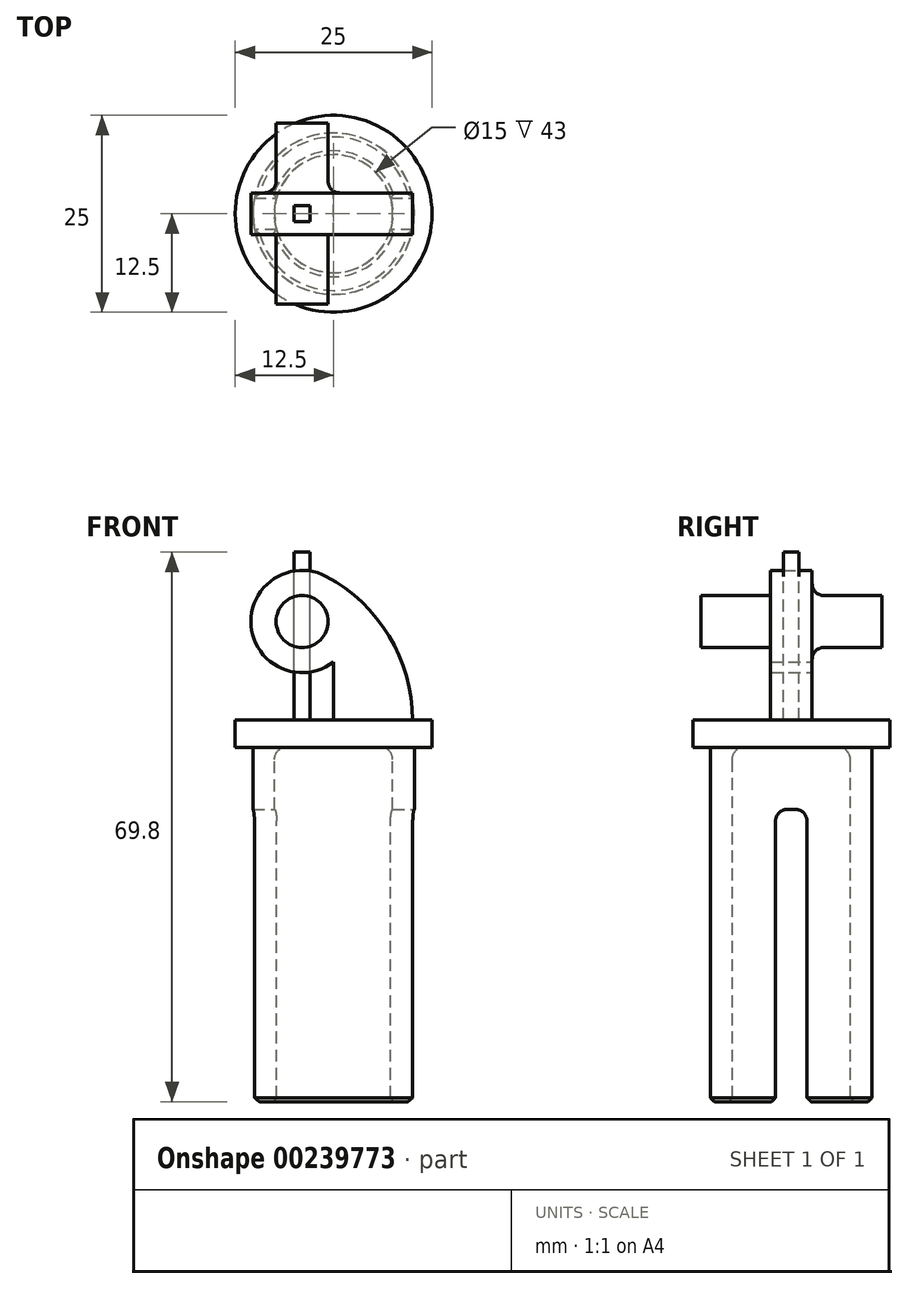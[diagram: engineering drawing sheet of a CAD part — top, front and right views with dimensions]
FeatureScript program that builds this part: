
annotation { "Feature Type Name" : "Feature", "Feature Type Description" : "" }
export const myFeature = defineFeature(function(context is Context, id is Id, definition is map)
    precondition{}
    {
        {
            var Q0;
            Q0=qCreatedBy(makeId("Front.planeOp"),FACE);
            var sketch = newSketch(context, id + "F0", { "sketchPlane" : qUnion([Q0])});
            skCircle(sketch, "E0", {"center": v(-4, 12.5) * mm, "radius": 3.3 * mm});
            skCircle(sketch, "E1", {"center": v(-4, 12.5) * mm, "radius": 6.5 * mm});
            skLineSegment(sketch, "E2.bottom", {"start": v(-4, 12.5) * mm, "end": v(0, 12.5) * mm});
            skLineSegment(sketch, "E2.top", {"start": v(-4, 0) * mm, "end": v(0, 0) * mm});
            skLineSegment(sketch, "E2.left", {"start": v(-4, 12.5) * mm, "end": v(-4, 0) * mm});
            skLineSegment(sketch, "E2.right", {"start": v(0, 12.5) * mm, "end": v(0, 0) * mm});
            skLineSegment(sketch, "E3.bottom", {"start": v(-4, 0) * mm, "end": v(10, 0) * mm});
            skLineSegment(sketch, "E3.top", {"start": v(-4, 19) * mm, "end": v(10, 19) * mm});
            skLineSegment(sketch, "E3.left", {"start": v(-4, 0) * mm, "end": v(-4, 19) * mm});
            skLineSegment(sketch, "E3.right", {"start": v(10, 0) * mm, "end": v(10, 19) * mm});
            skCircle(sketch, "E4", {"center": v(-10.67, 0) * mm, "radius": 20.67 * mm});
            skLineSegment(sketch, "E5", {"start": v(0, -28.46) * mm, "end": v(0, 52.46) * mm, "construction": true});
            skLineSegment(sketch, "E6", {"start": v(-4, 12.5) * mm, "end": v(0, 12.5) * mm, "construction": true});
            skLineSegment(sketch, "E7", {"start": v(-54.91, 0) * mm, "end": v(33.58, 0) * mm, "construction": true});
            skSolve(sketch);
        }
        {
            var Q0;
            {var subQ3=sQuery(id+"F0.wireOp",EDGE,"E4");var subQ6=sQuery(id+"F0.wireOp",EDGE,"E1");var subQ9=makeQuery(id+"F0.imprint","INTERSECT",VERTEX,{"derivedFrom":[subQ6,subQ3]});Q0=makeQuery(id+"F0.imprint","IMPRINT",FACE,{"disambiguationData":[TD([[makeQuery(id+"F0.imprint","IMPRINT",EDGE,{"disambiguationData":[TD([[subQ9,1.0]])],"derivedFrom":subQ6}),-1.0]])]});}
            var Q1;
            {var subQ3=sQuery(id+"F0.wireOp",EDGE,"E0");var subQ8=sQuery(id+"F0.wireOp",EDGE,"E3.left");var subQ10=makeQuery(id+"F0.imprint","INTERSECT",VERTEX,{"disambiguationData":[OD(0.0)],"derivedFrom":[subQ3,subQ8]});Q1=makeQuery(id+"F0.imprint","IMPRINT",FACE,{"disambiguationData":[TD([[makeQuery(id+"F0.imprint","IMPRINT",EDGE,{"disambiguationData":[TD([[subQ10,1.0]])],"derivedFrom":subQ3}),-1.0]])]});}
            var Q2;
            {var subQ1=sQuery(id+"F0.wireOp",EDGE,"E2.bottom");var subQ5=sQuery(id+"F0.wireOp",EDGE,"E0");var subQ6=makeQuery(id+"F0.imprint","INTERSECT",VERTEX,{"derivedFrom":[subQ5,subQ1]});Q2=makeQuery(id+"F0.imprint","IMPRINT",FACE,{"disambiguationData":[TD([[makeQuery(id+"F0.imprint","IMPRINT",EDGE,{"disambiguationData":[TD([[subQ6,1.0]])],"derivedFrom":subQ5}),-1.0]])]});}
            var Q3;
            {var subQ0=sQuery(id+"F0.wireOp",EDGE,"E3.left");var subQ1=sQuery(id+"F0.wireOp",EDGE,"E0");var subQ2=makeQuery(id+"F0.imprint","INTERSECT",VERTEX,{"disambiguationData":[OD(0.0)],"derivedFrom":[subQ1,subQ0]});Q3=makeQuery(id+"F0.imprint","IMPRINT",FACE,{"disambiguationData":[TD([[makeQuery(id+"F0.imprint","IMPRINT",EDGE,{"disambiguationData":[TD([[subQ2,-1.0]])],"derivedFrom":subQ1}),-1.0]])]});}
            extrude(context, id + "F1", {"entities" : qUnion([Q0, Q1, Q2, Q3]), "endBound" : BoundingType.SYMMETRIC, "depth" : 5.3 * mm});
        }
        {
            var Q0;
            {var subQ0=sQuery(id+"F0.wireOp",EDGE,"E2.bottom");var subQ1=sQuery(id+"F0.wireOp",EDGE,"E0");var subQ2=makeQuery(id+"F0.imprint","INTERSECT",VERTEX,{"derivedFrom":[subQ1,subQ0]});Q0=makeQuery(id+"F0.imprint","IMPRINT",FACE,{"disambiguationData":[TD([[makeQuery(id+"F0.imprint","IMPRINT",EDGE,{"disambiguationData":[TD([[subQ2,1.0]])],"derivedFrom":subQ1}),1.0]])]});}
            var Q1;
            {var subQ0=sQuery(id+"F0.wireOp",EDGE,"E3.left");var subQ1=sQuery(id+"F0.wireOp",EDGE,"E0");var subQ2=makeQuery(id+"F0.imprint","INTERSECT",VERTEX,{"disambiguationData":[OD(0.0)],"derivedFrom":[subQ1,subQ0]});Q1=makeQuery(id+"F0.imprint","IMPRINT",FACE,{"disambiguationData":[TD([[makeQuery(id+"F0.imprint","IMPRINT",EDGE,{"disambiguationData":[TD([[subQ2,1.0]])],"derivedFrom":subQ1}),1.0]])]});}
            var Q2;
            {var subQ0=sQuery(id+"F0.wireOp",EDGE,"E3.left");var subQ1=sQuery(id+"F0.wireOp",EDGE,"E0");var subQ2=makeQuery(id+"F0.imprint","INTERSECT",VERTEX,{"disambiguationData":[OD(0.0)],"derivedFrom":[subQ1,subQ0]});Q2=makeQuery(id+"F0.imprint","IMPRINT",FACE,{"disambiguationData":[TD([[makeQuery(id+"F0.imprint","IMPRINT",EDGE,{"disambiguationData":[TD([[subQ2,-1.0]])],"derivedFrom":subQ1}),1.0]])]});}
            extrude(context, id + "F2", {"entities" : qUnion([Q0, Q1, Q2]), "operationType" : NewBodyOperationType.ADD, "endBound" : BoundingType.SYMMETRIC, "depth" : 23 * mm});
        }
        {
            var Q0;
            Q0=qCreatedBy(makeId("Top.planeOp"),FACE);
            var sketch = newSketch(context, id + "F3", { "sketchPlane" : qUnion([Q0])});
            skCircle(sketch, "E8", {"center": v(0, 0) * mm, "radius": 12.5 * mm});
            skSolve(sketch);
        }
        {
            var Q0;
            Q0=makeQuery(id+"F3.imprint","IMPRINT",FACE,{"disambiguationData":[TD([[makeQuery(id+"F3.imprint","IMPRINT",EDGE,{"derivedFrom":sQuery(id+"F3.wireOp",EDGE,"E8")}),1.0]])]});
            extrude(context, id + "F4", {"entities" : qUnion([Q0]), "operationType" : NewBodyOperationType.ADD, "oppositeDirection" : true, "depth" : 3.5 * mm});
        }
        {
            var Q0;
            Q0=makeQuery(id+"F4.opExtrude","CAP_FACE",FACE,{"disambiguationData":[OSD([sQuery(id+"F3.wireOp",EDGE,"E8")])],"isStart":false});
            var sketch = newSketch(context, id + "F5", { "sketchPlane" : qUnion([Q0])});
            skCircle(sketch, "E9", {"center": v(0, 0) * mm, "radius": 10.25 * mm});
            skCircle(sketch, "E10", {"center": v(0, 0) * mm, "radius": 7.5 * mm});
            skSolve(sketch);
        }
        {
            var Q0;
            Q0=makeQuery(id+"F5.imprint","IMPRINT",FACE,{"disambiguationData":[TD([[makeQuery(id+"F5.imprint","IMPRINT",EDGE,{"derivedFrom":sQuery(id+"F5.wireOp",EDGE,"E9")}),1.0]])]});
            extrude(context, id + "F6", {"entities" : qUnion([Q0]), "operationType" : NewBodyOperationType.ADD, "depth" : 45 * mm, "offsetDistance" : 25 * mm});
        }
        {
            var Q0;
            Q0=qCreatedBy(makeId("Front.planeOp"),FACE);
            var sketch = newSketch(context, id + "F7", { "sketchPlane" : qUnion([Q0])});
            skLineSegment(sketch, "E11.bottom", {"start": v(-22.97, -55.7) * mm, "end": v(29.36, -55.7) * mm});
            skLineSegment(sketch, "E11.top", {"start": v(-22.97, -11.36) * mm, "end": v(29.36, -11.36) * mm});
            skLineSegment(sketch, "E11.left", {"start": v(-22.97, -55.7) * mm, "end": v(-22.97, -11.36) * mm});
            skLineSegment(sketch, "E11.right", {"start": v(29.36, -55.7) * mm, "end": v(29.36, -11.36) * mm});
            skSolve(sketch);
        }
        {
            var Q0;
            Q0=makeQuery(id+"F7.imprint","IMPRINT",FACE,{"disambiguationData":[TD([[makeQuery(id+"F7.imprint","IMPRINT",EDGE,{"derivedFrom":sQuery(id+"F7.wireOp",EDGE,"E11.bottom")}),1.0]])]});
            extrude(context, id + "F8", {"entities" : qUnion([Q0]), "operationType" : NewBodyOperationType.REMOVE, "endBound" : BoundingType.SYMMETRIC, "depth" : 4 * mm, "offsetDistance" : 25 * mm});
        }
        {
            var Q0;
            Q0=makeQuery(id+"F1.opExtrude","CAP_EDGE",EDGE,{"disambiguationData":[OSD([sQuery(id+"F0.wireOp",EDGE,"E3.bottom")])],"isStart":false});
            var Q1;
            Q1=makeQuery(id+"F1.opExtrude","CAP_EDGE",EDGE,{"disambiguationData":[OSD([sQuery(id+"F0.wireOp",EDGE,"E0")])],"isStart":false});
            var Q2;
            Q2=makeQuery(id+"F1.opExtrude","CAP_EDGE",EDGE,{"disambiguationData":[OSD([sQuery(id+"F0.wireOp",EDGE,"E0")])],"isStart":true});
            var Q3;
            Q3=makeQuery(id+"F1.opExtrude","SWEPT_EDGE",EDGE,{"disambiguationData":[OSD([sQuery(id+"F0.wireOp",EDGE,"E2.right"),sQuery(id+"F0.wireOp",EDGE,"E3.bottom")])]});
            var Q4;
            Q4=makeQuery(id+"F6.opExtrude","CAP_EDGE",EDGE,{"disambiguationData":[OSD([sQuery(id+"F5.wireOp",EDGE,"E9")])],"isStart":true});
            var Q5;
            Q5=makeQuery(id+"F1.opExtrude","CAP_EDGE",EDGE,{"disambiguationData":[OSD([sQuery(id+"F0.wireOp",EDGE,"E3.bottom")])],"isStart":true});
            var Q6;
            Q6=makeQuery(id+"F1.opExtrude","SWEPT_EDGE",EDGE,{"disambiguationData":[OSD([sQuery(id+"F0.wireOp",EDGE,"E3.bottom"),sQuery(id+"F0.wireOp",EDGE,"E3.right"),sQuery(id+"F0.wireOp",EDGE,"E4")])]});
            var Q7;
            Q7=makeQuery(id+"F6.boolean.opBoolean","SPLIT",FACE,{"disambiguationData":[TD([makeQuery(id+"F6.opExtrude","SWEPT_FACE",FACE,{"disambiguationData":[OSD([sQuery(id+"F5.wireOp",EDGE,"E10")])]})])],"derivedFrom":makeQuery(id+"F4.opExtrude","CAP_FACE",FACE,{"disambiguationData":[OSD([sQuery(id+"F3.wireOp",EDGE,"E8")])],"isStart":false})});
            var Q8;
            Q8=makeQuery(id+"F8.boolean.opBoolean","COPY",EDGE,{"disambiguationData":[OD(0.0)],"derivedFrom":makeQuery(id+"F8.opExtrude","CAP_EDGE",EDGE,{"disambiguationData":[OSD([sQuery(id+"F7.wireOp",EDGE,"E11.top")])],"isStart":true})});
            var Q9;
            Q9=makeQuery(id+"F8.boolean.opBoolean","COPY",EDGE,{"disambiguationData":[OD(0.0)],"derivedFrom":makeQuery(id+"F8.opExtrude","CAP_EDGE",EDGE,{"disambiguationData":[OSD([sQuery(id+"F7.wireOp",EDGE,"E11.top")])],"isStart":false})});
            var Q10;
            Q10=makeQuery(id+"F8.boolean.opBoolean","COPY",EDGE,{"disambiguationData":[OD(1.0)],"derivedFrom":makeQuery(id+"F8.opExtrude","CAP_EDGE",EDGE,{"disambiguationData":[OSD([sQuery(id+"F7.wireOp",EDGE,"E11.top")])],"isStart":false})});
            var Q11;
            Q11=makeQuery(id+"F8.boolean.opBoolean","COPY",EDGE,{"disambiguationData":[OD(1.0)],"derivedFrom":makeQuery(id+"F8.opExtrude","CAP_EDGE",EDGE,{"disambiguationData":[OSD([sQuery(id+"F7.wireOp",EDGE,"E11.top")])],"isStart":true})});
            fillet(context, id + "F9", {"entities" : qUnion([Q0, Q1, Q2, Q3, Q4, Q5, Q6, Q7, Q8, Q9, Q10, Q11]), "radius" : 1.5 * mm, "tangentPropagation" : true, "allowEdgeOverflow" : false});
        }
        {
            var Q0;
            {var subQ0=sQuery(id+"F5.wireOp",EDGE,"E9");var subQ1=sQuery(id+"F5.wireOp",EDGE,"E10");Q0=makeQuery(id+"F8.boolean.opBoolean","SPLIT",FACE,{"disambiguationData":[TD([makeQuery(id+"F8.opExtrude","CAP_FACE",FACE,{"disambiguationData":[OSD([sQuery(id+"F7.wireOp",EDGE,"E11.bottom"),sQuery(id+"F7.wireOp",EDGE,"E11.top"),sQuery(id+"F7.wireOp",EDGE,"E11.left"),sQuery(id+"F7.wireOp",EDGE,"E11.right")])],"isStart":true})])],"derivedFrom":makeQuery(id+"F6.opExtrude","CAP_FACE",FACE,{"disambiguationData":[OSD([subQ0,subQ1])],"isStart":false})});}
            var Q1;
            {var subQ0=sQuery(id+"F5.wireOp",EDGE,"E9");var subQ1=sQuery(id+"F5.wireOp",EDGE,"E10");Q1=makeQuery(id+"F8.boolean.opBoolean","SPLIT",FACE,{"disambiguationData":[TD([makeQuery(id+"F8.opExtrude","CAP_FACE",FACE,{"disambiguationData":[OSD([sQuery(id+"F7.wireOp",EDGE,"E11.bottom"),sQuery(id+"F7.wireOp",EDGE,"E11.top"),sQuery(id+"F7.wireOp",EDGE,"E11.left"),sQuery(id+"F7.wireOp",EDGE,"E11.right")])],"isStart":false})])],"derivedFrom":makeQuery(id+"F6.opExtrude","CAP_FACE",FACE,{"disambiguationData":[OSD([subQ0,subQ1])],"isStart":false})});}
            chamfer(context, id + "F13", {"entities" : qUnion([Q0, Q1]), "width" : 0.5 * mm, "tangentPropagation" : true});
        }
        {
            var Q0;
            Q0=makeQuery(id+"F4.opExtrude","CAP_FACE",FACE,{"disambiguationData":[OSD([sQuery(id+"F3.wireOp",EDGE,"E8")])],"isStart":true});
            cPlane(context, id + "F10", {"entities" : qUnion([Q0]), "cplaneType" : CPlaneType.OFFSET, "offset" : 21.3 * mm, "width" : 150 * mm, "height" : 150 * mm});
        }
        {
            var Q0;
            Q0=qCreatedBy(id+"F10.planeOp",FACE);
            var sketch = newSketch(context, id + "F11", { "sketchPlane" : qUnion([Q0])});
            skLineSegment(sketch, "E12.0", {"start": v(-0.7, 11.5) * mm, "end": v(-7.3, 11.5) * mm, "construction": true});
            skLineSegment(sketch, "E13.0", {"start": v(-0.7, -11.5) * mm, "end": v(-7.3, -11.5) * mm, "construction": true});
            skLineSegment(sketch, "E14.0.0", {"start": v(-10.5, 2.65) * mm, "end": v(0, 2.65) * mm, "construction": true});
            skLineSegment(sketch, "E14.0.1", {"start": v(0, 2.65) * mm, "end": v(0, -2.65) * mm, "construction": true});
            skLineSegment(sketch, "E14.0.2", {"start": v(0, -2.65) * mm, "end": v(-10.5, -2.65) * mm, "construction": true});
            skLineSegment(sketch, "E14.0.3", {"start": v(-0.94, -2.65) * mm, "end": v(-0.94, 2.65) * mm, "construction": true});
            skLineSegment(sketch, "E15.0.0", {"start": v(-0.94, -2.65) * mm, "end": v(9.95, -2.65) * mm, "construction": true});
            skFitSpline(sketch, "E15.0.1", {"points": [v(9.95, -2.65) * mm, v(9.95, -2.65) * mm, v(9.95, -2.65) * mm, v(9.95, -2.65) * mm], "construction": true});
            skLineSegment(sketch, "E15.0.2", {"start": v(9.95, -2.65) * mm, "end": v(9.95, 2.65) * mm, "construction": true});
            skFitSpline(sketch, "E15.0.3", {"points": [v(9.95, 2.65) * mm, v(9.95, 2.65) * mm, v(9.95, 2.65) * mm, v(9.95, 2.65) * mm], "construction": true});
            skLineSegment(sketch, "E15.0.4", {"start": v(9.95, 2.65) * mm, "end": v(-0.94, 2.65) * mm, "construction": true});
            skLineSegment(sketch, "E15.0.5", {"start": v(-0.94, 2.65) * mm, "end": v(-0.94, -2.65) * mm, "construction": true});
            skLineSegment(sketch, "E16", {"start": v(-4, 11.5) * mm, "end": v(-4, -11.5) * mm});
            skLineSegment(sketch, "E17", {"start": v(9.95, 0) * mm, "end": v(-10.5, 0) * mm});
            skArc(sketch, "E18.0.startCap", {"start": v(-5, 11.5) * mm, "mid": v(-4, 12.5) * mm, "end": v(-3, 11.5) * mm});
            skArc(sketch, "E18.0.endCap", {"start": v(-3, -11.5) * mm, "mid": v(-4, -12.5) * mm, "end": v(-5, -11.5) * mm});
            skLineSegment(sketch, "E18.0.left", {"start": v(-3, 11.5) * mm, "end": v(-3, -11.5) * mm});
            skLineSegment(sketch, "E18.0.right", {"start": v(-5, 11.5) * mm, "end": v(-5, -11.5) * mm});
            skArc(sketch, "E18.1.startCap", {"start": v(9.95, 1) * mm, "mid": v(10.95, 0) * mm, "end": v(9.95, -1) * mm});
            skArc(sketch, "E18.1.endCap", {"start": v(-10.5, -1) * mm, "mid": v(-11.5, 0) * mm, "end": v(-10.5, 1) * mm});
            skLineSegment(sketch, "E18.1.left", {"start": v(9.95, -1) * mm, "end": v(-10.5, -1) * mm});
            skLineSegment(sketch, "E18.1.right", {"start": v(9.95, 1) * mm, "end": v(-10.5, 1) * mm});
            skSolve(sketch);
        }
        {
            var Q0;
            {var subQ1=sQuery(id+"F11.wireOp",EDGE,"E18.1.startCap");Q0=makeQuery(id+"F11.imprint","IMPRINT",FACE,{"disambiguationData":[TD([[makeQuery(id+"F11.imprint","IMPRINT",EDGE,{"derivedFrom":subQ1}),-1.0]])]});}
            var Q1;
            {var subQ1=sQuery(id+"F11.wireOp",EDGE,"E18.1.endCap");Q1=makeQuery(id+"F11.imprint","IMPRINT",FACE,{"disambiguationData":[TD([[makeQuery(id+"F11.imprint","IMPRINT",EDGE,{"derivedFrom":subQ1}),-1.0]])]});}
            var Q2;
            {var subQ0=sQuery(id+"F11.wireOp",EDGE,"E18.1.left");var subQ1=sQuery(id+"F11.wireOp",EDGE,"E16");var subQ2=makeQuery(id+"F11.imprint","INTERSECT",VERTEX,{"derivedFrom":[subQ1,subQ0]});Q2=makeQuery(id+"F11.imprint","IMPRINT",FACE,{"disambiguationData":[TD([[makeQuery(id+"F11.imprint","IMPRINT",EDGE,{"disambiguationData":[TD([[subQ2,1.0]])],"derivedFrom":subQ1}),-1.0]])]});}
            var Q3;
            {var subQ0=sQuery(id+"F11.wireOp",EDGE,"E18.1.left");var subQ1=sQuery(id+"F11.wireOp",EDGE,"E16");var subQ2=makeQuery(id+"F11.imprint","INTERSECT",VERTEX,{"derivedFrom":[subQ1,subQ0]});Q3=makeQuery(id+"F11.imprint","IMPRINT",FACE,{"disambiguationData":[TD([[makeQuery(id+"F11.imprint","IMPRINT",EDGE,{"disambiguationData":[TD([[subQ2,1.0]])],"derivedFrom":subQ1}),1.0]])]});}
            var Q4;
            {var subQ0=sQuery(id+"F11.wireOp",EDGE,"E18.1.right");var subQ1=sQuery(id+"F11.wireOp",EDGE,"E16");var subQ2=makeQuery(id+"F11.imprint","INTERSECT",VERTEX,{"derivedFrom":[subQ1,subQ0]});Q4=makeQuery(id+"F11.imprint","IMPRINT",FACE,{"disambiguationData":[TD([[makeQuery(id+"F11.imprint","IMPRINT",EDGE,{"disambiguationData":[TD([[subQ2,-1.0]])],"derivedFrom":subQ1}),1.0]])]});}
            var Q5;
            {var subQ0=sQuery(id+"F11.wireOp",EDGE,"E18.1.right");var subQ1=sQuery(id+"F11.wireOp",EDGE,"E16");var subQ2=makeQuery(id+"F11.imprint","INTERSECT",VERTEX,{"derivedFrom":[subQ1,subQ0]});Q5=makeQuery(id+"F11.imprint","IMPRINT",FACE,{"disambiguationData":[TD([[makeQuery(id+"F11.imprint","IMPRINT",EDGE,{"disambiguationData":[TD([[subQ2,-1.0]])],"derivedFrom":subQ1}),-1.0]])]});}
            var Q6;
            {var subQ1=sQuery(id+"F11.wireOp",EDGE,"E18.0.startCap");Q6=makeQuery(id+"F11.imprint","IMPRINT",FACE,{"disambiguationData":[TD([[makeQuery(id+"F11.imprint","IMPRINT",EDGE,{"derivedFrom":subQ1}),-1.0]])]});}
            var Q7;
            {var subQ5=sQuery(id+"F11.wireOp",EDGE,"E18.0.endCap");Q7=makeQuery(id+"F11.imprint","IMPRINT",FACE,{"disambiguationData":[TD([[makeQuery(id+"F11.imprint","IMPRINT",EDGE,{"derivedFrom":subQ5}),-1.0]])]});}
            var Q8;
            Q8=makeQuery(id+"F4.opExtrude","CAP_FACE",FACE,{"disambiguationData":[OSD([sQuery(id+"F3.wireOp",EDGE,"E8")])],"isStart":true});
            extrude(context, id + "F12", {"entities" : qUnion([Q0, Q1, Q2, Q3, Q4, Q5, Q6, Q7]), "endBound" : BoundingType.UP_TO_SURFACE, "oppositeDirection" : true, "depth" : 25 * mm, "endBoundEntityFace" : qUnion([Q8]), "offsetDistance" : 25 * mm});
        }
    });
